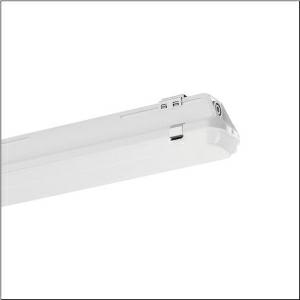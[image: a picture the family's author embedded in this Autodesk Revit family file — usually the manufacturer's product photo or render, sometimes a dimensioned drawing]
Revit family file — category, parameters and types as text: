
# Revit family: monsun_r__21_51fb107p430j_33ee
name_source: partatom
category: Lighting Fixtures
units: mm (PartAtom-declared; Revit-internal decimal feet)

## family parameters
Cut with Voids When Loaded = No
Host = Face
Light Source = No
Part Type = Normal
Room Calculation Point = No
Round Connector Dimension = Use Diameter
Shared = No

## types (1)
- Monsun® 21 (1 x LED, 3710 lm, 22.2 W, 4000K)
    Apparent Load = 22 VA
    CIE Flux Codes = 47 77 93 94 100
    Color Rendering = 80
    Color Temperature = 4000K
    Default Elevation = 1800 mm
    Description = Monsun® 21, damp-proof luminaire, chain hanger, primary optical cover: enclosure, of PMMA, light emission: direct distribution, primary light characteristic: symmetric, installation type: suspended mounting, surface-mounted, horizontal mounting, vertical mounting, LED, rated luminous flux: 3.710lm, luminous efficacy: 167lm/W, light colour: 840, colour temperature: 4000K, control gear: ECG, with terminal, 3-pole, max. 2.5mm², mains connection: 220..240V, AC, 50/60Hz, rated input power: 22W, housing, of glass-fibre reinforced polyester, uncoated, bright grey, length: 1.590mm, width: 90mm, height: 88mm, clip for enclosure, of stainless steel (V2A), ceiling mounting element, of stainless steel (V2A), chain hanger, of stainless steel (V2A), protection rating (complete): IP66, insulation class (complete): insulation class I (protective earthing), certification: CE, ENEC, VDE, UKCA, protection symbol: D, impact resistance: IK04, permissible operating ambient temperature: -25..+35°C, standard: EN 50419, EN 60598-2-1, corresponds to IFS (International Featured Standards) requirements for safety and quality in the food industry, for indoor or canopied outdoor use, no direct snow, no direct sun, no direct rain, packaging unit: 1 piece
    Height = 89 mm
    Lamp = 1 x LED
    Lamp Light Flux = 3710 lm
    Lamp Power = 22.2 W
    Lamp count = 1
    Length = 1590 mm
    Luminous efficacy = 167 lm/W
    Manufacturer = Siteco
    ModVariant = No
    Model = 51FB107P430J
    Mounting Place = Ceiling
    Mounting Type = Pendant
    Number of Poles = 1
    OnlyDefault = Yes
    Power Factor = 1
    Product Name = Monsun® 21
    Product group = damp-proof luminaire | ceiling pendant
    ProductGroupID = 908
    Protection Class = Protection class I
    Protection Degree = IP 66
    RLX_Detail_Level = 1
    RlxData = <blob elided: 88033 chars, md5=e3c73706>
    Socket = socket
    Standby Power = 0 W
    System Light Flux = 3710 lm
    System Power = 22 W
    Type Comments = Product without accessories
    Type Image = l_1006717.jpg
    URL = http://relux.com
    VarID = ---
    Voltage = 0 V
    Weight = 0.00 kg
    Width = 90 mm

## geometry (parser evidence)
native form markers: Blend x4, Sweep x14
no freeform markers — native parametric forms only
